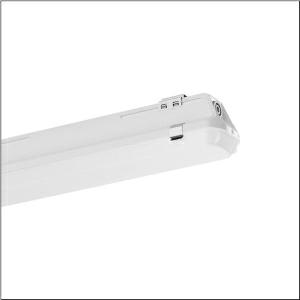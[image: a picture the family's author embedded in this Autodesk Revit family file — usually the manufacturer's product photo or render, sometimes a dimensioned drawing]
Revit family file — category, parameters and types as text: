
# Revit family: monsun_r__11_51fp10fp460h_036e
name_source: partatom
category: Lighting Fixtures
units: mm (PartAtom-declared; Revit-internal decimal feet)

## family parameters
Cut with Voids When Loaded = No
Host = Face
Light Source = No
Part Type = Normal
Room Calculation Point = No
Round Connector Dimension = Use Diameter
Shared = No

## types (1)
- --- (1 x LED, 6050 lm, 34.6 W, 4000K)
    Apparent Load = 35 VA
    CIE Flux Codes = 47 77 93 94 100
    Color Rendering = 80
    Color Temperature = 4000K
    Default Elevation = 1800 mm
    Description = Monsun® 11, damp-proof luminaire, chain hanger, primary optical cover: enclosure, of PMMA, light emission: direct distribution, primary light characteristic: symmetric, installation type: suspended mounting, surface-mounted, horizontal mounting, vertical mounting, LED, rated luminous flux: 6.050lm, luminous efficacy: 175lm/W, light colour: 840, colour temperature: 4000K, control gear: ECG DALI, with terminal, 5-pole, max. 2.5mm², mains connection: 220..240V, AC, 50/60Hz, start of lifetime: 35W, end of service life: 39W, luminaire housing, of glass-fibre reinforced polyester, uncoated, bright grey, incl. chain hanger, length: 1.590mm, width: 90mm, height: 88mm, clip for enclosure, of stainless steel (V2A), ceiling mounting element, of stainless steel (V2A), chain hanger, of stainless steel (V2A), protection rating (complete): IP66, insulation class (complete): insulation class I (protective earthing), certification: CE, ENEC, VDE, UKCA, protection symbol: D, impact resistance: IK04, permissible operating ambient temperature: -25..+40°C, standard: EN 50419, EN 60598-2-1, no direct snow, no direct sun, no direct rain, for indoor or canopied outdoor use, corresponds to IFS (International Featured Standards) requirements for safety and quality in the food industry, contact your sales advisor before using the luminaires in applications with unclear chemical exposure, large temperature fluctuations or condensation-forming humidity, LABS conformity tested according to VDMA 24364:2018-05, packaging unit: 1 piece
    Height = 89 mm
    Lamp = 1 x LED
    Lamp Light Flux = 6050 lm
    Lamp Power = 34.6 W
    Lamp count = 1
    Length = 1590 mm
    Luminous efficacy = 175 lm/W
    Manufacturer = Siteco
    ModVariant = No
    Model = 51FP10FP460H
    Mounting Place = Ceiling
    Mounting Type = Surface mounted
    Number of Poles = 1
    OnlyDefault = Yes
    Power Factor = 1
    Product Name = Monsun® 11
    Product group = damp-proof luminaire
    ProductGroupID = 300
    Protection Class = Protection class I
    Protection Degree = IP 66
    RLX_Detail_Level = 1
    RLX_Emergency_Light_Flux = 0 lm
    RLX_Emergency_Type = 0
    RLX_Emergency_Type_DB = No
    RlxData = <blob elided: 92385 chars, md5=6e55311b>
    Socket = socket
    Standby Power = 0 W
    System Light Flux = 6050 lm
    System Power = 35 W
    Type Comments = factory setting: luminous flux: 100 % | dim-lin: 254 | 232 mA
    Type Image = l_1004748.jpg
    URL = http://relux.com
    VarID = @adj_142393
    Voltage = 0 V
    Weight = 0.00 kg
    Width = 90 mm

## geometry (parser evidence)
native form markers: Blend x4, Sweep x14
no freeform markers — native parametric forms only
